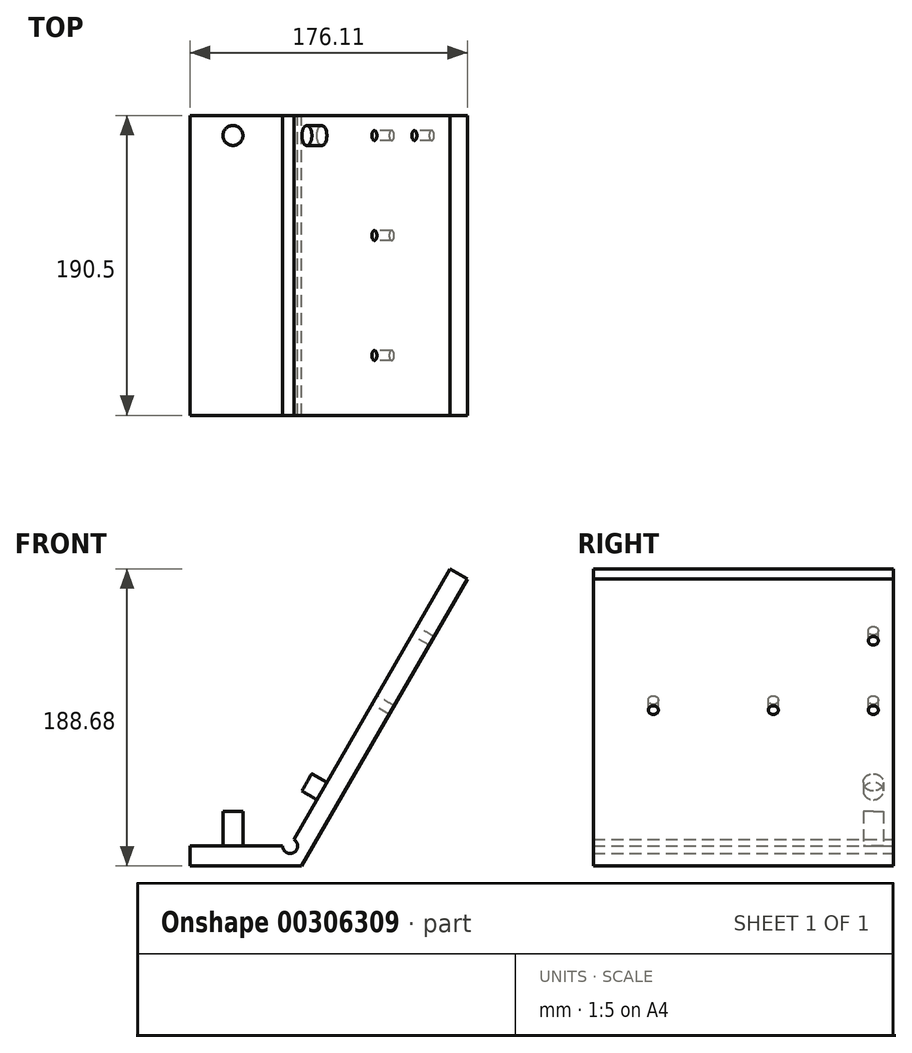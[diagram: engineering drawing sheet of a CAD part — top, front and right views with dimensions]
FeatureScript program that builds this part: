
annotation { "Feature Type Name" : "Feature", "Feature Type Description" : "" }
export const myFeature = defineFeature(function(context is Context, id is Id, definition is map)
    precondition{}
    {
        {
            var Q0;
            Q0=qCreatedBy(makeId("Front.planeOp"),FACE);
            var sketch = newSketch(context, id + "F0", { "sketchPlane" : qUnion([Q0])});
            skLineSegment(sketch, "E0", {"start": v(-50.6, 0) * mm, "end": v(-50.6, -12.7) * mm});
            skLineSegment(sketch, "E1", {"start": v(-50.6, -12.7) * mm, "end": v(20.23, -12.7) * mm});
            skLineSegment(sketch, "E2", {"start": v(20.23, -12.7) * mm, "end": v(125.5, 169.63) * mm});
            skLineSegment(sketch, "E3", {"start": v(125.5, 169.63) * mm, "end": v(114.5, 175.98) * mm});
            skLineSegment(sketch, "E4", {"start": v(114.5, 175.98) * mm, "end": v(15.28, 4.12) * mm});
            skArc(sketch, "E5", {"start": v(8.14, 0) * mm, "mid": v(15.28, -4.12) * mm, "end": v(15.28, 4.12) * mm});
            skLineSegment(sketch, "E6", {"start": v(8.14, 0) * mm, "end": v(-50.6, 0) * mm});
            skSolve(sketch);
        }
        {
            var Q0;
            Q0 = qSketchRegion(id + "F0", true);
            extrude(context, id + "F1", {"entities" : qUnion([Q0]), "depth" : 190.5 * mm});
        }
        {
            var Q0;
            Q0=makeQuery(id+"F1.opExtrude","SWEPT_FACE",FACE,{"disambiguationData":[OSD([sQuery(id+"F0.wireOp",EDGE,"E6")])]});
            var sketch = newSketch(context, id + "F2", { "sketchPlane" : qUnion([Q0])});
            skCircle(sketch, "E7", {"center": v(-23.43, -12.7) * mm, "radius": 6.35 * mm});
            skSolve(sketch);
        }
        {
            var Q0;
            Q0=makeQuery(id+"F2.imprint","IMPRINT",FACE,{"disambiguationData":[TD([[makeQuery(id+"F2.imprint","IMPRINT",EDGE,{"derivedFrom":sQuery(id+"F2.wireOp",EDGE,"E7")}),1.0]])]});
            extrude(context, id + "F3", {"entities" : qUnion([Q0]), "operationType" : NewBodyOperationType.ADD, "depth" : 22 * mm});
        }
        {
            var Q0;
            Q0=makeQuery(id+"F1.opExtrude","SWEPT_FACE",FACE,{"disambiguationData":[OSD([sQuery(id+"F0.wireOp",EDGE,"E4")])]});
            var sketch = newSketch(context, id + "F4", { "sketchPlane" : qUnion([Q0])});
            skCircle(sketch, "E8", {"center": v(152.4, 113.45) * mm, "radius": 3.18 * mm});
            skCircle(sketch, "E9", {"center": v(76.2, 113.45) * mm, "radius": 3.18 * mm});
            skCircle(sketch, "E10", {"center": v(12.7, 113.45) * mm, "radius": 3.18 * mm});
            skCircle(sketch, "E11", {"center": v(12.7, 164.25) * mm, "radius": 3.18 * mm});
            skSolve(sketch);
        }
        {
            var Q0;
            Q0=makeQuery(id+"F4.imprint","IMPRINT",FACE,{"disambiguationData":[TD([[makeQuery(id+"F4.imprint","IMPRINT",EDGE,{"derivedFrom":sQuery(id+"F4.wireOp",EDGE,"E8")}),1.0]])]});
            var Q1;
            Q1=makeQuery(id+"F4.imprint","IMPRINT",FACE,{"disambiguationData":[TD([[makeQuery(id+"F4.imprint","IMPRINT",EDGE,{"derivedFrom":sQuery(id+"F4.wireOp",EDGE,"E9")}),1.0]])]});
            var Q2;
            Q2=makeQuery(id+"F4.imprint","IMPRINT",FACE,{"disambiguationData":[TD([[makeQuery(id+"F4.imprint","IMPRINT",EDGE,{"derivedFrom":sQuery(id+"F4.wireOp",EDGE,"E10")}),1.0]])]});
            var Q3;
            Q3=makeQuery(id+"F4.imprint","IMPRINT",FACE,{"disambiguationData":[TD([[makeQuery(id+"F4.imprint","IMPRINT",EDGE,{"derivedFrom":sQuery(id+"F4.wireOp",EDGE,"E11")}),1.0]])]});
            extrude(context, id + "F5", {"entities" : qUnion([Q0, Q1, Q2, Q3]), "operationType" : NewBodyOperationType.REMOVE, "endBound" : BoundingType.THROUGH_ALL, "oppositeDirection" : true, "depth" : 25.4 * mm});
        }
        {
            var Q0;
            Q0=makeQuery(id+"F1.opExtrude","SWEPT_FACE",FACE,{"disambiguationData":[OSD([sQuery(id+"F0.wireOp",EDGE,"E4")])]});
            var sketch = newSketch(context, id + "F6", { "sketchPlane" : qUnion([Q0])});
            skCircle(sketch, "E12", {"center": v(12.7, 46.77) * mm, "radius": 6.35 * mm});
            skSolve(sketch);
        }
        {
            var Q0;
            Q0=makeQuery(id+"F6.imprint","IMPRINT",FACE,{"disambiguationData":[TD([[makeQuery(id+"F6.imprint","IMPRINT",EDGE,{"derivedFrom":sQuery(id+"F6.wireOp",EDGE,"E12")}),1.0]])]});
            extrude(context, id + "F7", {"entities" : qUnion([Q0]), "operationType" : NewBodyOperationType.ADD, "depth" : 11 * mm});
        }
    });
